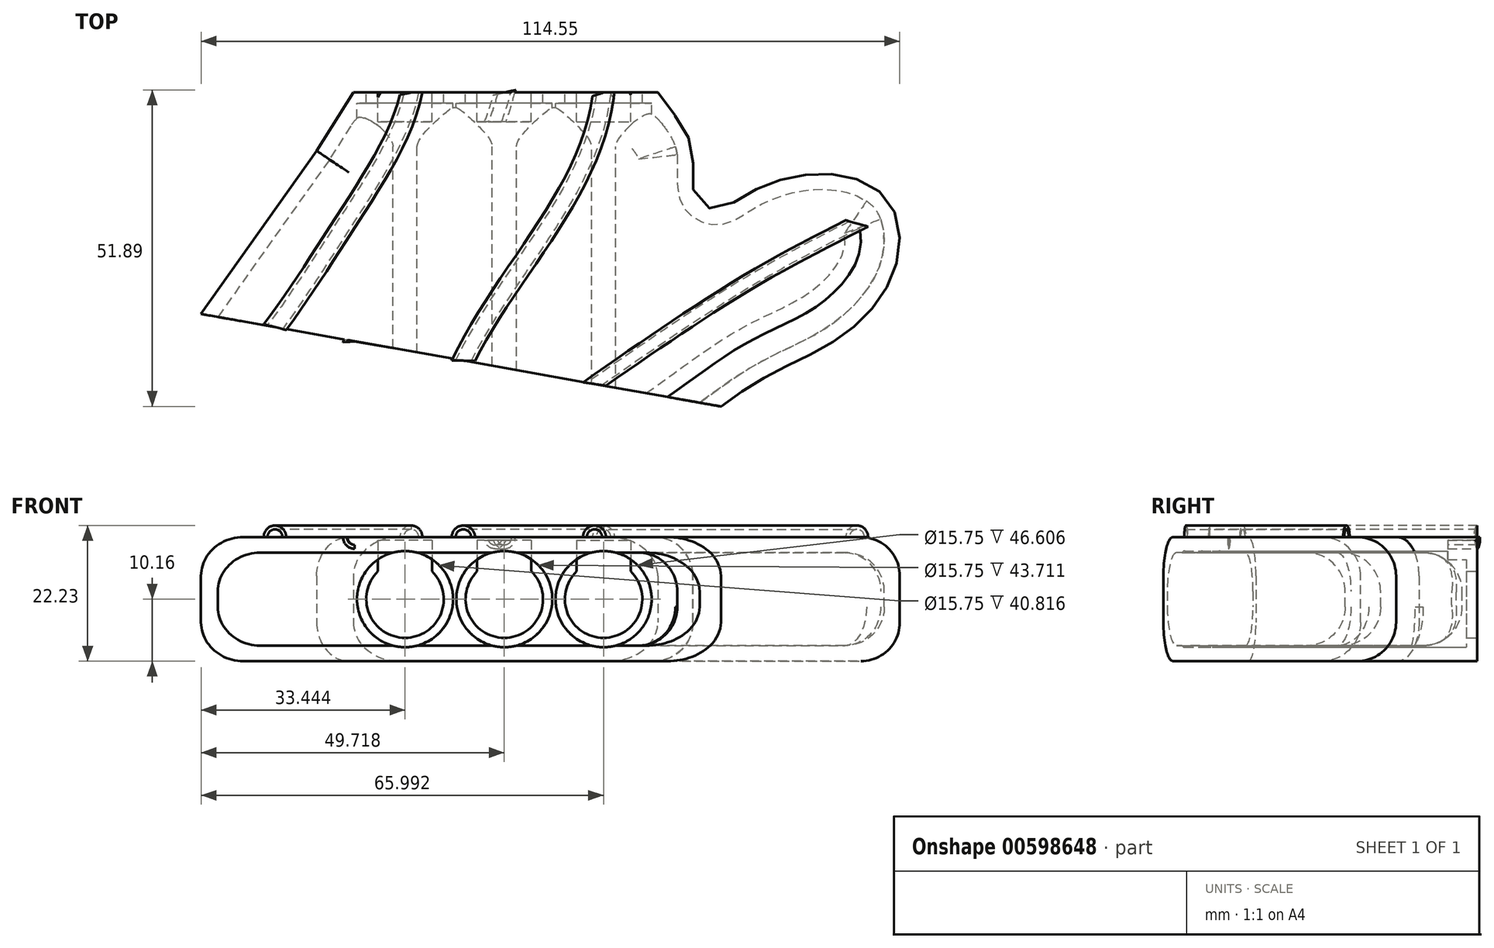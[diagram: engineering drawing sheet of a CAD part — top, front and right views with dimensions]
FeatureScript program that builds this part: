
annotation { "Feature Type Name" : "Feature", "Feature Type Description" : "" }
export const myFeature = defineFeature(function(context is Context, id is Id, definition is map)
    precondition{}
    {
        {
            var Q0;
            Q0=qCreatedBy(makeId("Top.planeOp"),FACE);
            var sketch = newSketch(context, id + "F0", { "sketchPlane" : qUnion([Q0])});
            skLineSegment(sketch, "E0", {"start": v(-2.53, 3.76) * mm, "end": v(-21.5, -22.97) * mm});
            skLineSegment(sketch, "E1", {"start": v(-21.5, -22.97) * mm, "end": v(63.73, -38.13) * mm});
            skFitSpline(sketch, "E2", {"points": [v(54.17, 12.07) * mm, v(59, 4.04) * mm, v(59.53, -3.66) * mm, v(63.11, -5.79) * mm, v(68.43, -3.13) * mm, v(80.08, 0) * mm, v(90.97, -4.14) * mm, v(92.29, -15.51) * mm, v(83.28, -26.78) * mm, v(72.06, -32.72) * mm, v(63.73, -38.13) * mm], "startDerivative": vector(65.3, -76.98) * mm, "endDerivative": vector(-77.9, -55.9) * mm});
            skLineSegment(sketch, "E3", {"start": v(53.4, 13.32) * mm, "end": v(3.5, 13.32) * mm});
            skLineSegment(sketch, "E4", {"start": v(3.5, 13.32) * mm, "end": v(-2.53, 3.76) * mm});
            skLineSegment(sketch, "E5", {"start": v(53.4, 13.32) * mm, "end": v(56.2, 9.58) * mm});
            skSolve(sketch);
        }
        {
            var Q0;
            Q0=makeQuery(id+"F0.imprint","IMPRINT",FACE,{"disambiguationData":[TD([[makeQuery(id+"F0.imprint","IMPRINT",EDGE,{"derivedFrom":sQuery(id+"F0.wireOp",EDGE,"E0")}),1.0]])]});
            extrude(context, id + "F1", {"entities" : qUnion([Q0]), "depth" : 20.32 * mm, "offsetDistance" : 25.4 * mm});
        }
        {
            var Q0;
            Q0=makeQuery(id+"F1.opExtrude","SWEPT_FACE",FACE,{"disambiguationData":[OSD([sQuery(id+"F0.wireOp",EDGE,"E1")])]});
            shell(context, id + "F2", {"entities" : qUnion([Q0]), "thickness" : 2.54 * mm});
        }
        {
            var Q0;
            {var subQ0=sQuery(id+"F0.wireOp",EDGE,"E2");Q0=makeQuery(id+"F2.opShell","OFFSET_EDGE",EDGE,{"disambiguationData":[OSD([subQ0]),TDD([makeQuery(id+"F1.opExtrude","CAP_EDGE",EDGE,{"disambiguationData":[OSD([subQ0])],"isStart":true})])]});}
            var Q1;
            Q1=makeQuery(id+"F2.opShell","OFFSET_EDGE",EDGE,{"disambiguationData":[OSD([sQuery(id+"F0.wireOp",EDGE,"E2"),sQuery(id+"F0.wireOp",EDGE,"E5")])]});
            var Q2;
            {var subQ0=sQuery(id+"F0.wireOp",EDGE,"E3");Q2=makeQuery(id+"F2.opShell","OFFSET_EDGE",EDGE,{"disambiguationData":[OSD([subQ0]),TDD([makeQuery(id+"F1.opExtrude","CAP_EDGE",EDGE,{"disambiguationData":[OSD([subQ0])],"isStart":true})])]});}
            var Q3;
            {var subQ0=sQuery(id+"F0.wireOp",EDGE,"E0");Q3=makeQuery(id+"F2.opShell","OFFSET_EDGE",EDGE,{"disambiguationData":[OSD([subQ0]),TDD([makeQuery(id+"F1.opExtrude","CAP_EDGE",EDGE,{"disambiguationData":[OSD([subQ0])],"isStart":true})])]});}
            var Q4;
            {var subQ0=sQuery(id+"F0.wireOp",EDGE,"E0");Q4=makeQuery(id+"F2.opShell","OFFSET_EDGE",EDGE,{"disambiguationData":[OSD([subQ0]),TDD([makeQuery(id+"F1.opExtrude","CAP_EDGE",EDGE,{"disambiguationData":[OSD([subQ0])],"isStart":false})])]});}
            var Q5;
            {var subQ0=sQuery(id+"F0.wireOp",EDGE,"E3");Q5=makeQuery(id+"F2.opShell","OFFSET_EDGE",EDGE,{"disambiguationData":[OSD([subQ0]),TDD([makeQuery(id+"F1.opExtrude","CAP_EDGE",EDGE,{"disambiguationData":[OSD([subQ0])],"isStart":false})])]});}
            var Q6;
            {var subQ0=sQuery(id+"F0.wireOp",EDGE,"E2");Q6=makeQuery(id+"F2.opShell","OFFSET_EDGE",EDGE,{"disambiguationData":[OSD([subQ0]),TDD([makeQuery(id+"F1.opExtrude","CAP_EDGE",EDGE,{"disambiguationData":[OSD([subQ0])],"isStart":false})])]});}
            var Q7;
            Q7=makeQuery(id+"F2.opShell","OFFSET_EDGE",EDGE,{"disambiguationData":[OSD([sQuery(id+"F0.wireOp",EDGE,"E3"),sQuery(id+"F0.wireOp",EDGE,"E5")])]});
            var Q8;
            Q8=makeQuery(id+"F2.opShell","OFFSET_EDGE",EDGE,{"disambiguationData":[OSD([sQuery(id+"F0.wireOp",EDGE,"E3"),sQuery(id+"F0.wireOp",EDGE,"E4")])]});
            var Q9;
            Q9=makeQuery(id+"F2.opShell","OFFSET_EDGE",EDGE,{"disambiguationData":[OSD([sQuery(id+"F0.wireOp",EDGE,"E0"),sQuery(id+"F0.wireOp",EDGE,"E4")])]});
            var Q10;
            {var subQ0=sQuery(id+"F0.wireOp",EDGE,"E5");Q10=makeQuery(id+"F2.opShell","OFFSET_EDGE",EDGE,{"disambiguationData":[OSD([subQ0]),TDD([makeQuery(id+"F1.opExtrude","CAP_EDGE",EDGE,{"disambiguationData":[OSD([subQ0])],"isStart":false})])]});}
            var Q11;
            {var subQ0=sQuery(id+"F0.wireOp",EDGE,"E5");Q11=makeQuery(id+"F2.opShell","OFFSET_EDGE",EDGE,{"disambiguationData":[OSD([subQ0]),TDD([makeQuery(id+"F1.opExtrude","CAP_EDGE",EDGE,{"disambiguationData":[OSD([subQ0])],"isStart":true})])]});}
            var Q12;
            {var subQ0=sQuery(id+"F0.wireOp",EDGE,"E4");Q12=makeQuery(id+"F2.opShell","OFFSET_EDGE",EDGE,{"disambiguationData":[OSD([subQ0]),TDD([makeQuery(id+"F1.opExtrude","CAP_EDGE",EDGE,{"disambiguationData":[OSD([subQ0])],"isStart":false})])]});}
            var Q13;
            {var subQ0=sQuery(id+"F0.wireOp",EDGE,"E4");Q13=makeQuery(id+"F2.opShell","OFFSET_EDGE",EDGE,{"disambiguationData":[OSD([subQ0]),TDD([makeQuery(id+"F1.opExtrude","CAP_EDGE",EDGE,{"disambiguationData":[OSD([subQ0])],"isStart":true})])]});}
            var Q14;
            Q14=makeQuery(id+"F1.opExtrude","CAP_EDGE",EDGE,{"disambiguationData":[OSD([sQuery(id+"F0.wireOp",EDGE,"E2")])],"isStart":false});
            var Q15;
            Q15=makeQuery(id+"F1.opExtrude","CAP_EDGE",EDGE,{"disambiguationData":[OSD([sQuery(id+"F0.wireOp",EDGE,"E5")])],"isStart":false});
            var Q16;
            Q16=makeQuery(id+"F1.opExtrude","CAP_EDGE",EDGE,{"disambiguationData":[OSD([sQuery(id+"F0.wireOp",EDGE,"E0")])],"isStart":false});
            var Q17;
            Q17=makeQuery(id+"F1.opExtrude","CAP_EDGE",EDGE,{"disambiguationData":[OSD([sQuery(id+"F0.wireOp",EDGE,"E4")])],"isStart":false});
            var Q18;
            Q18=makeQuery(id+"F1.opExtrude","CAP_EDGE",EDGE,{"disambiguationData":[OSD([sQuery(id+"F0.wireOp",EDGE,"E2")])],"isStart":true});
            var Q19;
            Q19=makeQuery(id+"F1.opExtrude","CAP_EDGE",EDGE,{"disambiguationData":[OSD([sQuery(id+"F0.wireOp",EDGE,"E5")])],"isStart":true});
            var Q20;
            Q20=makeQuery(id+"F1.opExtrude","SWEPT_EDGE",EDGE,{"disambiguationData":[OSD([sQuery(id+"F0.wireOp",EDGE,"E2"),sQuery(id+"F0.wireOp",EDGE,"E5")])]});
            var Q21;
            Q21=makeQuery(id+"F1.opExtrude","CAP_EDGE",EDGE,{"disambiguationData":[OSD([sQuery(id+"F0.wireOp",EDGE,"E0")])],"isStart":true});
            fillet(context, id + "F3", {"entities" : qUnion([Q0, Q1, Q2, Q3, Q4, Q5, Q6, Q7, Q8, Q9, Q10, Q11, Q12, Q13, Q14, Q15, Q16, Q17, Q18, Q19, Q20, Q21]), "radius" : 6.35 * mm, "tangentPropagation" : true, "allowEdgeOverflow" : false});
        }
        {
            var Q0;
            Q0=makeQuery(id+"F1.opExtrude","SWEPT_FACE",FACE,{"disambiguationData":[OSD([sQuery(id+"F0.wireOp",EDGE,"E3")])]});
            var sketch = newSketch(context, id + "F4", { "sketchPlane" : qUnion([Q0])});
            skCircle(sketch, "E6", {"center": v(-28.23, 10.16) * mm, "radius": 6.35 * mm});
            skCircle(sketch, "E7", {"center": v(-44.5, 10.16) * mm, "radius": 6.35 * mm});
            skCircle(sketch, "E8.MirrorC", {"center": v(-11.95, 10.16) * mm, "radius": 6.35 * mm});
            skSolve(sketch);
        }
        {
            var Q0;
            Q0 = qSketchRegion(id + "F4", true);
            extrude(context, id + "F5", {"entities" : qUnion([Q0]), "operationType" : NewBodyOperationType.REMOVE, "endBound" : BoundingType.THROUGH_ALL, "oppositeDirection" : true, "depth" : 25.4 * mm, "offsetDistance" : 25.4 * mm});
        }
        {
            var Q0;
            Q0=makeQuery(id+"F1.opExtrude","SWEPT_FACE",FACE,{"disambiguationData":[OSD([sQuery(id+"F0.wireOp",EDGE,"E3")])]});
            var sketch = newSketch(context, id + "F6", { "sketchPlane" : qUnion([Q0])});
            skCircle(sketch, "E9", {"center": v(-44.5, 10.16) * mm, "radius": 7.87 * mm});
            skCircle(sketch, "E10", {"center": v(-28.23, 10.16) * mm, "radius": 7.87 * mm});
            skCircle(sketch, "E11", {"center": v(-11.95, 10.16) * mm, "radius": 7.87 * mm});
            skSolve(sketch);
        }
        {
            var Q0;
            Q0=makeQuery(id+"F6.imprint","IMPRINT",FACE,{"disambiguationData":[TD([[makeQuery(id+"F6.imprint","IMPRINT",EDGE,{"derivedFrom":sQuery(id+"F6.wireOp",EDGE,"E9")}),-1.0]])]});
            cPlane(context, id + "F7", {"entities" : qUnion([Q0]), "cplaneType" : CPlaneType.OFFSET, "offset" : 1.78 * mm, "oppositeDirection" : true, "width" : 152.4 * mm, "height" : 152.4 * mm});
        }
        {
            var Q0;
            Q0=qCreatedBy(id+"F7.planeOp",FACE);
            var sketch = newSketch(context, id + "F8", { "sketchPlane" : qUnion([Q0])});
            skCircle(sketch, "E12", {"center": v(-44.5, 10.16) * mm, "radius": 7.87 * mm});
            skCircle(sketch, "E13", {"center": v(-28.23, 10.16) * mm, "radius": 7.87 * mm});
            skCircle(sketch, "E14", {"center": v(-11.95, 10.16) * mm, "radius": 7.87 * mm});
            skSolve(sketch);
        }
        {
            var Q0;
            Q0 = qSketchRegion(id + "F8", true);
            extrude(context, id + "F9", {"entities" : qUnion([Q0]), "operationType" : NewBodyOperationType.REMOVE, "endBound" : BoundingType.THROUGH_ALL, "oppositeDirection" : true, "depth" : 25.4 * mm, "offsetDistance" : 25.4 * mm});
        }
        {
            var Q0;
            Q0=makeQuery(id+"F1.opExtrude","SWEPT_FACE",FACE,{"disambiguationData":[OSD([sQuery(id+"F0.wireOp",EDGE,"E3")])]});
            var sketch = newSketch(context, id + "F10", { "sketchPlane" : qUnion([Q0])});
            skLineSegment(sketch, "E15", {"start": v(-28.23, 20.32) * mm, "end": v(-28.23, 0) * mm});
            skLineSegment(sketch, "E16", {"start": v(-28.23, 19.77) * mm, "end": v(-23.78, 19.77) * mm});
            skLineSegment(sketch, "E17", {"start": v(-23.78, 19.77) * mm, "end": v(-23.78, 14.7) * mm});
            skArc(sketch, "E18", {"start": v(-28.23, 16.51) * mm, "mid": v(-25.83, 16.04) * mm, "end": v(-23.78, 14.7) * mm});
            skArc(sketch, "E19.MirrorCS", {"start": v(-28.23, 16.51) * mm, "mid": v(-30.63, 16.04) * mm, "end": v(-32.67, 14.7) * mm});
            skLineSegment(sketch, "E20.MirrorCS", {"start": v(-28.23, 19.77) * mm, "end": v(-32.67, 19.77) * mm});
            skLineSegment(sketch, "E21.MirrorCS", {"start": v(-32.67, 19.77) * mm, "end": v(-32.67, 14.7) * mm});
            skLineSegment(sketch, "E22", {"start": v(-44.5, 19.77) * mm, "end": v(-40.06, 19.77) * mm});
            skLineSegment(sketch, "E23", {"start": v(-40.06, 19.77) * mm, "end": v(-40.06, 14.7) * mm});
            skArc(sketch, "E24", {"start": v(-44.5, 16.51) * mm, "mid": v(-42.1, 16.04) * mm, "end": v(-40.06, 14.7) * mm});
            skArc(sketch, "E25.MirrorCS", {"start": v(-44.5, 16.51) * mm, "mid": v(-46.9, 16.04) * mm, "end": v(-48.95, 14.7) * mm});
            skLineSegment(sketch, "E26.MirrorCS", {"start": v(-44.5, 19.77) * mm, "end": v(-48.95, 19.77) * mm});
            skLineSegment(sketch, "E27.MirrorCS", {"start": v(-48.95, 19.77) * mm, "end": v(-48.95, 14.7) * mm});
            skLineSegment(sketch, "E28", {"start": v(-11.95, 19.77) * mm, "end": v(-7.5, 19.77) * mm});
            skLineSegment(sketch, "E29", {"start": v(-7.5, 19.77) * mm, "end": v(-7.5, 14.7) * mm});
            skArc(sketch, "E30", {"start": v(-11.95, 16.5) * mm, "mid": v(-9.55, 16.04) * mm, "end": v(-7.5, 14.7) * mm});
            skArc(sketch, "E31.MirrorCS", {"start": v(-11.95, 16.5) * mm, "mid": v(-14.35, 16.04) * mm, "end": v(-16.4, 14.7) * mm});
            skLineSegment(sketch, "E32.MirrorCS", {"start": v(-11.95, 19.77) * mm, "end": v(-16.4, 19.77) * mm});
            skLineSegment(sketch, "E33.MirrorCS", {"start": v(-16.4, 19.77) * mm, "end": v(-16.4, 14.7) * mm});
            skSolve(sketch);
        }
        {
            var Q0;
            Q0 = qSketchRegion(id + "F10", true);
            extrude(context, id + "F11", {"entities" : qUnion([Q0]), "operationType" : NewBodyOperationType.REMOVE, "oppositeDirection" : true, "depth" : 4.83 * mm, "offsetDistance" : 25.4 * mm});
        }
        {
            var Q0;
            Q0=makeQuery(id+"F1.opExtrude","CAP_FACE",FACE,{"disambiguationData":[OSD([sQuery(id+"F0.wireOp",EDGE,"E0"),sQuery(id+"F0.wireOp",EDGE,"E1"),sQuery(id+"F0.wireOp",EDGE,"E2"),sQuery(id+"F0.wireOp",EDGE,"E3"),sQuery(id+"F0.wireOp",EDGE,"E4"),sQuery(id+"F0.wireOp",EDGE,"E5")])],"isStart":false});
            var sketch = newSketch(context, id + "F12", { "sketchPlane" : qUnion([Q0])});
            skFitSpline(sketch, "E34", {"points": [v(43, -34.44) * mm, v(67.48, -18.17) * mm, v(86.04, -8.14) * mm], "startDerivative": vector(46.49, 32.28) * mm, "endDerivative": vector(39.4, 20.02) * mm});
            skPoint(sketch, "E35", {"position": v(28.23, 13.32) * mm});
            skPoint(sketch, "E36", {"position": v(44.5, 13.32) * mm});
            skPoint(sketch, "E37", {"position": v(12.99, 13.32) * mm});
            skFitSpline(sketch, "E38", {"points": [v(12.99, 13.32) * mm, v(2.38, -7.62) * mm, v(-9.37, -25.12) * mm], "startDerivative": vector(-8.46, -41.08) * mm, "endDerivative": vector(-25.6, -34.2) * mm});
            skFitSpline(sketch, "E39", {"points": [v(28.23, 13.32) * mm, v(19.05, -5.05) * mm, v(3.69, -27.45) * mm], "startDerivative": vector(-10.67, -41.84) * mm, "endDerivative": vector(-18.82, -44.62) * mm});
            skFitSpline(sketch, "E40", {"points": [v(44.5, 13.32) * mm, v(35.55, -8.38) * mm, v(21.52, -30.62) * mm], "startDerivative": vector(-5.32, -48.42) * mm, "endDerivative": vector(-20.74, -42.96) * mm});
            skLineSegment(sketch, "E41", {"start": v(0, -11.31) * mm, "end": v(61.07, -22.18) * mm});
            skPoint(sketch, "E42", {"position": v(0, -11.31) * mm});
            skPoint(sketch, "E43", {"position": v(12.5, -13.54) * mm});
            skPoint(sketch, "E44", {"position": v(30, -16.65) * mm});
            skPoint(sketch, "E45", {"position": v(61.07, -22.18) * mm});
            skSolve(sketch);
        }
        {
            var Q0;
            Q0=makeQuery(id+"F1.opExtrude","SWEPT_FACE",FACE,{"disambiguationData":[OSD([sQuery(id+"F0.wireOp",EDGE,"E1")])]});
            cPlane(context, id + "F13", {"entities" : qUnion([Q0]), "cplaneType" : CPlaneType.OFFSET, "offset" : 15.24 * mm, "oppositeDirection" : true, "width" : 152.4 * mm, "height" : 152.4 * mm});
        }
        {
            var Q0;
            Q0=qCreatedBy(id+"F13.planeOp",FACE);
            var sketch = newSketch(context, id + "F14", { "sketchPlane" : qUnion([Q0])});
            skCircle(sketch, "E46", {"center": v(1.98, 20.32) * mm, "radius": 1.27 * mm});
            skCircle(sketch, "E47", {"center": v(14.68, 20.32) * mm, "radius": 1.27 * mm});
            skCircle(sketch, "E48", {"center": v(32.46, 20.32) * mm, "radius": 1.27 * mm});
            skCircle(sketch, "E49", {"center": v(1.98, 20.32) * mm, "radius": 1.9 * mm});
            skCircle(sketch, "E50", {"center": v(14.68, 20.32) * mm, "radius": 1.9 * mm});
            skCircle(sketch, "E51", {"center": v(32.46, 20.32) * mm, "radius": 1.9 * mm});
            skLineSegment(sketch, "E52", {"start": v(0.08, 20.32) * mm, "end": v(34.37, 20.32) * mm});
            skCircle(sketch, "E53", {"center": v(64.01, 20.32) * mm, "radius": 1.27 * mm});
            skCircle(sketch, "E54", {"center": v(64.01, 20.32) * mm, "radius": 1.9 * mm});
            skLineSegment(sketch, "E55", {"start": v(65.92, 20.32) * mm, "end": v(34.37, 20.32) * mm});
            skSolve(sketch);
        }
        {
            var Q0;
            {var subQ0=sQuery(id+"F14.wireOp",EDGE,"E52");var subQ1=sQuery(id+"F14.wireOp",EDGE,"E48");var subQ2=makeQuery(id+"F14.imprint","INTERSECT",VERTEX,{"disambiguationData":[OD(0.0)],"derivedFrom":[subQ1,subQ0]});Q0=makeQuery(id+"F14.imprint","IMPRINT",FACE,{"disambiguationData":[TD([[makeQuery(id+"F14.imprint","IMPRINT",EDGE,{"disambiguationData":[TD([[subQ2,1.0]])],"derivedFrom":subQ1}),-1.0]])]});}
            var Q1;
            Q1=sQuery(id+"F12.wireOp",EDGE,"E40");
            sweep(context, id + "F15", {"operationType" : NewBodyOperationType.ADD, "profiles" : qUnion([Q0]), "path" : qUnion([Q1])});
        }
        {
            var Q0;
            {var subQ0=sQuery(id+"F14.wireOp",EDGE,"E52");var subQ1=sQuery(id+"F14.wireOp",EDGE,"E47");var subQ2=makeQuery(id+"F14.imprint","INTERSECT",VERTEX,{"disambiguationData":[OD(0.0)],"derivedFrom":[subQ1,subQ0]});Q0=makeQuery(id+"F14.imprint","IMPRINT",FACE,{"disambiguationData":[TD([[makeQuery(id+"F14.imprint","IMPRINT",EDGE,{"disambiguationData":[TD([[subQ2,1.0]])],"derivedFrom":subQ1}),-1.0]])]});}
            var Q1;
            Q1=sQuery(id+"F12.wireOp",EDGE,"E39");
            sweep(context, id + "F16", {"operationType" : NewBodyOperationType.ADD, "profiles" : qUnion([Q0]), "path" : qUnion([Q1])});
        }
        {
            var Q0;
            {var subQ0=sQuery(id+"F14.wireOp",EDGE,"E52");var subQ1=sQuery(id+"F14.wireOp",EDGE,"E46");var subQ2=makeQuery(id+"F14.imprint","INTERSECT",VERTEX,{"disambiguationData":[OD(0.0)],"derivedFrom":[subQ1,subQ0]});Q0=makeQuery(id+"F14.imprint","IMPRINT",FACE,{"disambiguationData":[TD([[makeQuery(id+"F14.imprint","IMPRINT",EDGE,{"disambiguationData":[TD([[subQ2,1.0]])],"derivedFrom":subQ1}),-1.0]])]});}
            var Q1;
            Q1=sQuery(id+"F12.wireOp",EDGE,"E38");
            sweep(context, id + "F17", {"operationType" : NewBodyOperationType.ADD, "profiles" : qUnion([Q0]), "path" : qUnion([Q1])});
        }
        {
            var Q0;
            {var subQ0=sQuery(id+"F12.wireOp",EDGE,"E39");Q0=makeQuery(id+"F12.imprint","IMPRINT",FACE,{"disambiguationData":[TD([[makeQuery(id+"F12.imprint","IMPRINT",EDGE,{"derivedFrom":subQ0}),1.0]])]});}
            var sketch = newSketch(context, id + "F18", { "sketchPlane" : qUnion([Q0])});
            skLineSegment(sketch, "E56", {"start": v(44.5, 13.32) * mm, "end": v(46.47, 13.32) * mm});
            skLineSegment(sketch, "E57", {"start": v(46.47, 13.32) * mm, "end": v(46.38, 13.98) * mm});
            skLineSegment(sketch, "E58", {"start": v(46.38, 13.98) * mm, "end": v(13.16, 13.73) * mm});
            skLineSegment(sketch, "E59", {"start": v(13.16, 13.73) * mm, "end": v(12.93, 13.32) * mm});
            skLineSegment(sketch, "E60", {"start": v(12.93, 13.32) * mm, "end": v(46.47, 13.32) * mm});
            skSolve(sketch);
        }
        {
            var Q0;
            Q0 = qSketchRegion(id + "F18", true);
            extrude(context, id + "F19", {"entities" : qUnion([Q0]), "operationType" : NewBodyOperationType.REMOVE, "endBound" : BoundingType.THROUGH_ALL, "depth" : 25.4 * mm, "offsetDistance" : 25.4 * mm});
        }
        {
            var Q0;
            {var subQ0=sQuery(id+"F14.wireOp",EDGE,"E55");var subQ1=sQuery(id+"F14.wireOp",EDGE,"E53");var subQ2=makeQuery(id+"F14.imprint","INTERSECT",VERTEX,{"disambiguationData":[OD(0.0)],"derivedFrom":[subQ1,subQ0]});Q0=makeQuery(id+"F14.imprint","IMPRINT",FACE,{"disambiguationData":[TD([[makeQuery(id+"F14.imprint","IMPRINT",EDGE,{"disambiguationData":[TD([[subQ2,-1.0]])],"derivedFrom":subQ1}),-1.0]])]});}
            var Q1;
            Q1=sQuery(id+"F12.wireOp",EDGE,"E34");
            sweep(context, id + "F20", {"operationType" : NewBodyOperationType.ADD, "profiles" : qUnion([Q0]), "path" : qUnion([Q1])});
        }
    });
